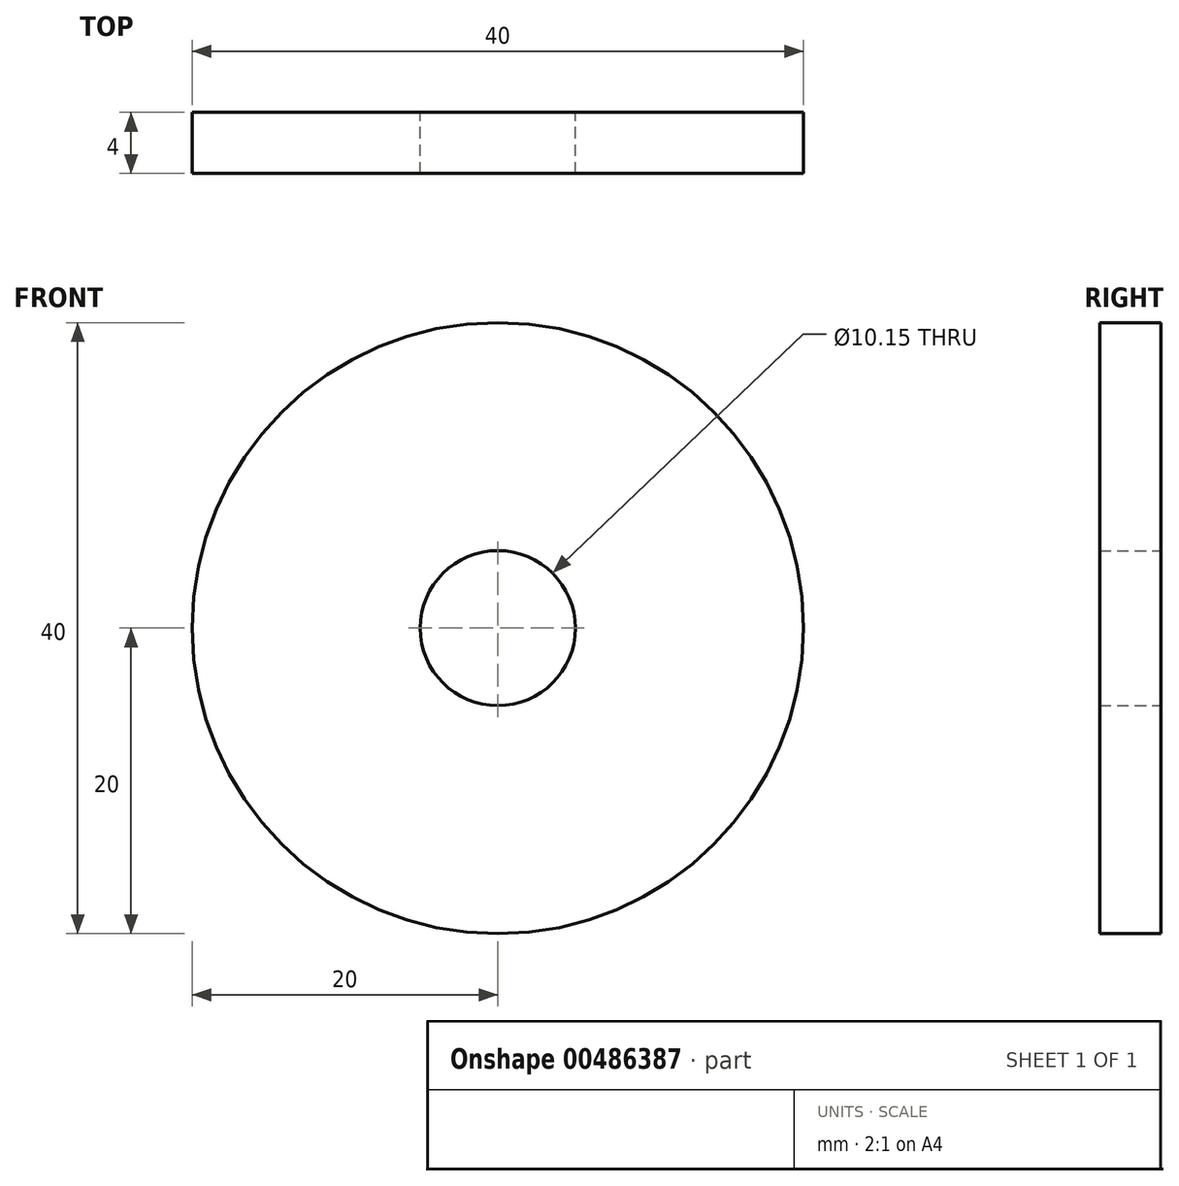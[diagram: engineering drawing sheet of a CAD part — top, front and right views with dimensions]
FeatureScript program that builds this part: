
annotation { "Feature Type Name" : "Feature", "Feature Type Description" : "" }
export const myFeature = defineFeature(function(context is Context, id is Id, definition is map)
    precondition{}
    {
        {
            var Q0;
            Q0=qCreatedBy(makeId("Front.planeOp"),FACE);
            var sketch = newSketch(context, id + "F0", { "sketchPlane" : qUnion([Q0])});
            skCircle(sketch, "E0", {"center": v(0, 0) * mm, "radius": 5.08 * mm});
            skCircle(sketch, "E1", {"center": v(0, 0) * mm, "radius": 20 * mm});
            skSolve(sketch);
        }
        {
            var Q0;
            Q0=makeQuery(id+"F0.imprint","IMPRINT",FACE,{"disambiguationData":[TD([[makeQuery(id+"F0.imprint","IMPRINT",EDGE,{"derivedFrom":sQuery(id+"F0.wireOp",EDGE,"E0")}),-1.0]])]});
            extrude(context, id + "F1", {"entities" : qUnion([Q0]), "depth" : 4 * mm});
        }
    });
